# Revit family: DSP_A3-Kal-Aluminium-Sliding-Single-2100w
name_source: partatom
category: Doors
revit_build: Autodesk Revit 2016 (Build: 20150220_1215(x64)
units: mm (PartAtom-declared; Revit-internal decimal feet)

## family parameters
Always vertical = Yes
Cut with Voids When Loaded = No
Host = Wall
Room Calculation Point = No
Shared = No

## types (1)
- 2100w X 2100h
    Assembly Code = B2030110
    Construction Type = Aluminium
    Frame Finish = Anodised Aluminium
    Function = Interior
    Height = 2100 mm  [stored 6.88976 ft]
    Manufacturer = Kal-Aluminium
    Manufacturer Code = 2100 FS
    Material Door Frame = Default Aluminium Door Frame
    Material Glass = Glass
    Model = Arcadia Patio Doors
    Model Type = Single Sliding
    Rough Height = 0 mm  [stored 0 ft]
    Rough Width = 0 mm  [stored 0 ft]
    Thickness = 0 mm  [stored 0 ft]
    URL = http://www.kal.co.za
    Wall Closure = By host
    Width = 2100 mm  [stored 6.88976 ft]

note: [stored X ft] marks values corroborated as IEEE doubles in the binary element streams (Revit-internal decimal feet)

## geometry (parser evidence)
native form markers: Sweep x6
no freeform markers — native parametric forms only
